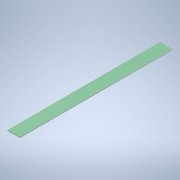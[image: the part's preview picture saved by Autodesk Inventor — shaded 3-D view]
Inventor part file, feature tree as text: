
AUTODESK INVENTOR PART (.ipt)
format: ipt  version: 2022 (Build 260153000, 153)  size: 95,232 bytes
history: native  units: mm
features: other x1, extrude x1, sketch x1
ambient origin geometry x8: Origin, YZ Plane, XZ Plane, XY Plane, X Axis, Y Axis, Z Axis, Center Point
bodies: Body1 (feature_tree)
feature tree (3):
  other  "ソリッド1"
  extrude  "押し出し1"  Depth=360.0mm
  sketch  "スケッチ1"
